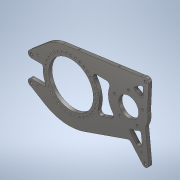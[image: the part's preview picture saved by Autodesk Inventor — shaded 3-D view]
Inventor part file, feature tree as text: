
AUTODESK INVENTOR PART (.ipt)
format: ipt  version: 2021 (Build 250183000, 183)  size: 535,552 bytes
history: native  units: in
note: dims shown in document units (in); Inventor stores cm internally (conversion verified against a paired STEP export)
features: sketch x17, extrude x12, fillet x7, hole x6, chamfer x1, projected_geometry x1
ambient origin geometry x8: Origin, YZ Plane, XZ Plane, XY Plane, X Axis, Y Axis, Z Axis, Center Point
bodies: Body1 (feature_tree)
feature tree (44):
  extrude  "Extrusion13"  Depth=0.5in TaperAngle=0.0deg
  hole  "Hole4"  [1 undecoded]
  extrude  "Extrusion15"  Depth=1.0in
  extrude  "Extrusion17"  Depth=0.5in TaperAngle=0.0deg
  hole  "Hole9"  [1 undecoded]
  hole  "Hole10"  [1 undecoded]
  extrude  "Extrusion18"  Depth=1.0in
  extrude  "Extrusion19"  Depth=0.239in
  extrude  "Extrusion24"  Depth=0.5in
  fillet  "Fillet3"  Radius=0.1718in
  extrude  "Extrusion27"  Depth=0.75in
  chamfer  "Chamfer1"  Distance=1.0in
  sketch  "Sketch40"  dims[d194=0.3526in d197=0.239in]
  extrude  "Extrusion29"  Depth=0.5in TaperAngle=0.0deg
  extrude  "Extrusion30"  Depth=0.75in
  fillet  "Fillet4"  Radius=1.0in
  fillet  "Fillet5"  Radius=0.75in
  extrude  "Extrusion32"  Depth=0.75in
  extrude  "Extrusion35"  Depth=0.5in
  fillet  "Fillet6"  Radius=2.8in
  fillet  "Fillet7"  Radius=0.25in
  extrude  "Extrusion36"  Depth=0.5in
  fillet  "Fillet8"  Radius=1.0in
  hole  "Hole11"  [1 undecoded]
  hole  "Hole12"  [1 undecoded]
  hole  "Hole14"  [1 undecoded]
  fillet  "Fillet9"  Radius=1.0in
  sketch  "Sketch14"  dims[d96=8.5in d97=2.16in d98=9.0in d99=5.5in d100=1.0in d101=1.0in d102=6.0in d103=6.0in d104=3.718in d105=1.0in d108=10.718in d109=1.5in d111=0.5in d112=0.0in]
  sketch  "Sketch15"  dims[d113=0.386in d114=0.75in d115=0.762in d116=0.25in d117=0.5635in d118=0.484in d119=0.8108in d132=5.0in]
  sketch  "Sketch18"  dims[d133=17.223in d134=1.0in]
  sketch  "Sketch21"  dims[d135=1.0in d136=0.5in d137=0.0in]
  sketch  "Sketch29"  dims[d155=1.0in d156=0.0in d178=7.75in]
  sketch  "Sketch31"  dims[d179=3.5433in d181=360.0deg]
  sketch  "Sketch32"  dims[d183=0.257in d184=0.75in d185=0.438in d186=0.25in d187=0.5635in d188=1.0in d189=0.8108in d191=1.0in]
  sketch  "Sketch39"  dims[d192=0.0481in d193=1.0in]
  sketch  "Sketch42"  dims[d198=0.1195in d199=0.5in]
  sketch  "Sketch43"  dims[d200=0.266in d201=0.75in d202=0.507in d203=0.25in d204=0.5635in d205=1.0in d206=0.8108in d207=0.1718in]
  sketch  "Sketch45"  dims[d208=15.0deg d210=0.75in]
  sketch  "Sketch48"  dims[d211=0.75in]
  sketch  "Sketch49"  dims[d212=0.75in]
  sketch  "Sketch50"  dims[d213=0.25in]
  sketch  "Sketch51"  dims[d214=0.5in d215=1.0in d216=0.0in]
  sketch  "Sketch54"  dims[d217=0.25in d218=1.0in d219=0.0in d223=0.75in d242=1.0in d243=0.0in d247=0.75in d249=0.75in d250=0.5in d251=2.8in d262=0.25in d263=0.5in d264=1.0in d265=0.0in d266=0.0156in d267=0.125in d268=45.0deg d284=1.0in d285=0.0in d296=6.75in d297=1.0in d298=0.0in d303=3.005in d304=8.715in d305=6.5in d306=0.5in d307=0.5in d308=4.44in d309=0.325in d310=1.9685in d312=360.0deg d314=1.0in d315=0.0in d317=0.061in d332=0.055in d333=0.5in d334=0.0in d335=11.5in d336=5.0in d337=3.0in d338=10.0in d339=0.5in d340=0.0in d341=7.0in d342=0.25in d343=2.0in d346=0.196in d347=0.5in d348=0.375in d349=0.25in d350=0.5635in d351=0.65in d352=0.8108in d353=2.25in d354=8.375in d355=0.25in d356=0.196in d357=0.5in d358=0.375in d359=0.25in d360=0.5635in d361=0.65in d362=0.8108in d370=0.25in d371=1.75in d372=0.196in d373=0.5in d374=0.375in d375=0.25in d376=0.5635in d377=0.65in d378=0.8108in d379=3.0in d283=0.5in d286=0.0344in]
  projected_geometry  "Project Cut Edges1"
note: 6 required parameter values undecoded (feature->parameter linkage not recoverable at this tier; creation-order binding heuristic only, values carry confidence <= 0.55)
